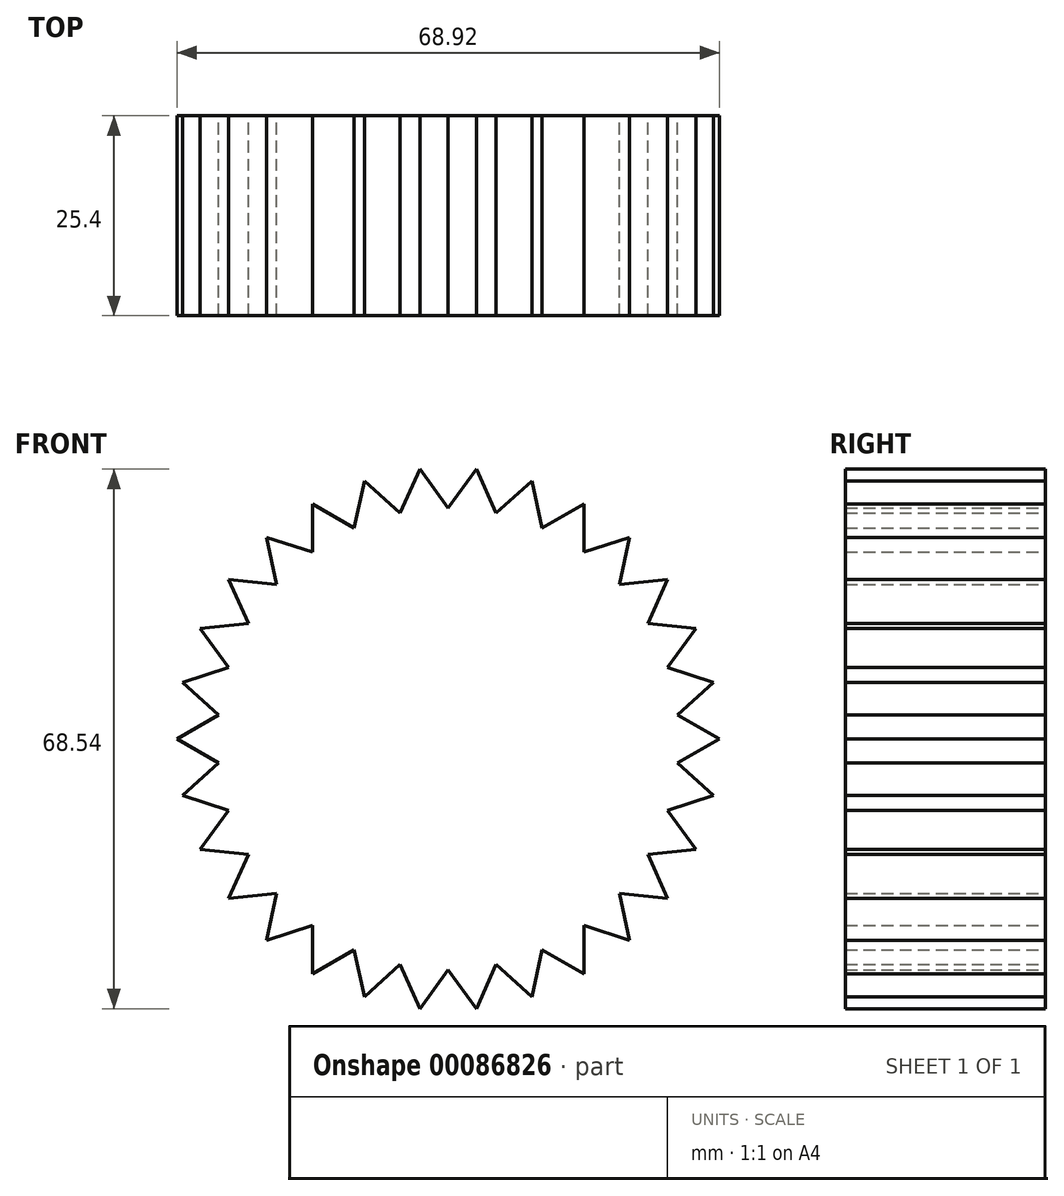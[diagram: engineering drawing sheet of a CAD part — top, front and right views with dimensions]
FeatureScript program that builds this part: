
annotation { "Feature Type Name" : "Feature", "Feature Type Description" : "" }
export const myFeature = defineFeature(function(context is Context, id is Id, definition is map)
    precondition{}
    {
        {
            var Q0;
            Q0=qCreatedBy(makeId("Front.planeOp"),FACE);
            var sketch = newSketch(context, id + "F0", { "sketchPlane" : qUnion([Q0])});
            skCircle(sketch, "E0.cCircle", {"center": v(0, 0) * mm, "radius": 29.31 * mm, "construction": true});
            skLineSegment(sketch, "E0.0", {"start": v(0, 29.31) * mm, "end": v(6.1, 28.67) * mm, "construction": true});
            skLineSegment(sketch, "E0.1", {"start": v(6.1, 28.67) * mm, "end": v(11.92, 26.78) * mm, "construction": true});
            skLineSegment(sketch, "E0.2", {"start": v(11.92, 26.78) * mm, "end": v(17.23, 23.71) * mm, "construction": true});
            skLineSegment(sketch, "E0.3", {"start": v(17.23, 23.71) * mm, "end": v(21.78, 19.61) * mm, "construction": true});
            skLineSegment(sketch, "E0.4", {"start": v(21.78, 19.61) * mm, "end": v(25.38, 14.66) * mm, "construction": true});
            skLineSegment(sketch, "E0.5", {"start": v(25.38, 14.66) * mm, "end": v(27.88, 9.06) * mm, "construction": true});
            skLineSegment(sketch, "E0.6", {"start": v(27.88, 9.06) * mm, "end": v(29.15, 3.06) * mm, "construction": true});
            skLineSegment(sketch, "E0.7", {"start": v(29.15, 3.06) * mm, "end": v(29.15, -3.06) * mm, "construction": true});
            skLineSegment(sketch, "E0.8", {"start": v(29.15, -3.06) * mm, "end": v(27.88, -9.06) * mm, "construction": true});
            skLineSegment(sketch, "E0.9", {"start": v(27.88, -9.06) * mm, "end": v(25.38, -14.66) * mm, "construction": true});
            skLineSegment(sketch, "E0.10", {"start": v(25.38, -14.66) * mm, "end": v(21.78, -19.61) * mm, "construction": true});
            skLineSegment(sketch, "E0.11", {"start": v(21.78, -19.61) * mm, "end": v(17.23, -23.71) * mm, "construction": true});
            skLineSegment(sketch, "E0.12", {"start": v(17.23, -23.71) * mm, "end": v(11.92, -26.78) * mm, "construction": true});
            skLineSegment(sketch, "E0.13", {"start": v(11.92, -26.78) * mm, "end": v(6.1, -28.67) * mm, "construction": true});
            skLineSegment(sketch, "E0.14", {"start": v(6.1, -28.67) * mm, "end": v(0, -29.31) * mm, "construction": true});
            skLineSegment(sketch, "E0.15", {"start": v(0, -29.31) * mm, "end": v(-6.1, -28.67) * mm, "construction": true});
            skLineSegment(sketch, "E0.16", {"start": v(-6.1, -28.67) * mm, "end": v(-11.92, -26.78) * mm, "construction": true});
            skLineSegment(sketch, "E0.17", {"start": v(-11.92, -26.78) * mm, "end": v(-17.23, -23.71) * mm, "construction": true});
            skLineSegment(sketch, "E0.18", {"start": v(-17.23, -23.71) * mm, "end": v(-21.78, -19.61) * mm, "construction": true});
            skLineSegment(sketch, "E0.19", {"start": v(-21.78, -19.61) * mm, "end": v(-25.38, -14.66) * mm, "construction": true});
            skLineSegment(sketch, "E0.20", {"start": v(-25.38, -14.66) * mm, "end": v(-27.88, -9.06) * mm, "construction": true});
            skLineSegment(sketch, "E0.21", {"start": v(-27.88, -9.06) * mm, "end": v(-29.15, -3.06) * mm, "construction": true});
            skLineSegment(sketch, "E0.22", {"start": v(-29.15, -3.06) * mm, "end": v(-29.15, 3.06) * mm, "construction": true});
            skLineSegment(sketch, "E0.23", {"start": v(-29.15, 3.06) * mm, "end": v(-27.88, 9.06) * mm, "construction": true});
            skLineSegment(sketch, "E0.24", {"start": v(-27.88, 9.06) * mm, "end": v(-25.38, 14.66) * mm, "construction": true});
            skLineSegment(sketch, "E0.25", {"start": v(-25.38, 14.66) * mm, "end": v(-21.78, 19.61) * mm, "construction": true});
            skLineSegment(sketch, "E0.26", {"start": v(-21.78, 19.61) * mm, "end": v(-17.23, 23.71) * mm, "construction": true});
            skLineSegment(sketch, "E0.27", {"start": v(-17.23, 23.71) * mm, "end": v(-11.92, 26.78) * mm, "construction": true});
            skLineSegment(sketch, "E0.28", {"start": v(-11.92, 26.78) * mm, "end": v(-6.1, 28.67) * mm, "construction": true});
            skLineSegment(sketch, "E0.29", {"start": v(-6.1, 28.67) * mm, "end": v(0, 29.31) * mm, "construction": true});
            skLineSegment(sketch, "E1", {"start": v(6.1, 28.67) * mm, "end": v(3.6, 34.27) * mm});
            skLineSegment(sketch, "E2", {"start": v(3.6, 34.27) * mm, "end": v(0, 29.31) * mm});
            skLineSegment(sketch, "E3.1.0", {"start": v(11.92, 26.78) * mm, "end": v(10.65, 32.77) * mm});
            skLineSegment(sketch, "E3.1.1", {"start": v(10.65, 32.77) * mm, "end": v(6.1, 28.67) * mm});
            skLineSegment(sketch, "E3.2.0", {"start": v(17.23, 23.71) * mm, "end": v(17.23, 29.84) * mm});
            skLineSegment(sketch, "E3.2.1", {"start": v(17.23, 29.84) * mm, "end": v(11.92, 26.78) * mm});
            skLineSegment(sketch, "E3.3.0", {"start": v(21.78, 19.61) * mm, "end": v(23.06, 25.6) * mm});
            skLineSegment(sketch, "E3.3.1", {"start": v(23.06, 25.6) * mm, "end": v(17.23, 23.71) * mm});
            skLineSegment(sketch, "E3.4.0", {"start": v(25.38, 14.66) * mm, "end": v(27.88, 20.25) * mm});
            skLineSegment(sketch, "E3.4.1", {"start": v(27.88, 20.25) * mm, "end": v(21.78, 19.61) * mm});
            skLineSegment(sketch, "E3.5.0", {"start": v(27.88, 9.06) * mm, "end": v(31.48, 14.01) * mm});
            skLineSegment(sketch, "E3.5.1", {"start": v(31.48, 14.01) * mm, "end": v(25.38, 14.66) * mm});
            skLineSegment(sketch, "E3.6.0", {"start": v(29.15, 3.06) * mm, "end": v(33.7, 7.16) * mm});
            skLineSegment(sketch, "E3.6.1", {"start": v(33.7, 7.16) * mm, "end": v(27.88, 9.06) * mm});
            skLineSegment(sketch, "E3.7.0", {"start": v(29.15, -3.06) * mm, "end": v(34.46, 0) * mm});
            skLineSegment(sketch, "E3.7.1", {"start": v(34.46, 0) * mm, "end": v(29.15, 3.06) * mm});
            skLineSegment(sketch, "E3.8.0", {"start": v(27.88, -9.06) * mm, "end": v(33.7, -7.16) * mm});
            skLineSegment(sketch, "E3.8.1", {"start": v(33.7, -7.16) * mm, "end": v(29.15, -3.06) * mm});
            skLineSegment(sketch, "E3.9.0", {"start": v(25.38, -14.66) * mm, "end": v(31.48, -14.01) * mm});
            skLineSegment(sketch, "E3.9.1", {"start": v(31.48, -14.01) * mm, "end": v(27.88, -9.06) * mm});
            skLineSegment(sketch, "E3.anchor1", {"start": v(0, 0) * mm, "end": v(6.1, 28.67) * mm, "construction": true});
            skLineSegment(sketch, "E3.anchor2", {"start": v(0, 0) * mm, "end": v(25.38, -14.66) * mm, "construction": true});
            skLineSegment(sketch, "E4.1.0", {"start": v(21.78, -19.61) * mm, "end": v(27.88, -20.25) * mm});
            skLineSegment(sketch, "E4.1.1", {"start": v(27.88, -20.25) * mm, "end": v(25.38, -14.66) * mm});
            skLineSegment(sketch, "E4.2.0", {"start": v(17.23, -23.71) * mm, "end": v(23.06, -25.6) * mm});
            skLineSegment(sketch, "E4.2.1", {"start": v(23.06, -25.6) * mm, "end": v(21.78, -19.61) * mm});
            skLineSegment(sketch, "E4.3.0", {"start": v(11.92, -26.78) * mm, "end": v(17.23, -29.84) * mm});
            skLineSegment(sketch, "E4.3.1", {"start": v(17.23, -29.84) * mm, "end": v(17.23, -23.71) * mm});
            skLineSegment(sketch, "E4.4.0", {"start": v(6.1, -28.67) * mm, "end": v(10.65, -32.77) * mm});
            skLineSegment(sketch, "E4.4.1", {"start": v(10.65, -32.77) * mm, "end": v(11.92, -26.78) * mm});
            skLineSegment(sketch, "E4.5.0", {"start": v(0, -29.31) * mm, "end": v(3.6, -34.27) * mm});
            skLineSegment(sketch, "E4.5.1", {"start": v(3.6, -34.27) * mm, "end": v(6.1, -28.67) * mm});
            skLineSegment(sketch, "E4.6.0", {"start": v(-6.1, -28.67) * mm, "end": v(-3.6, -34.27) * mm});
            skLineSegment(sketch, "E4.6.1", {"start": v(-3.6, -34.27) * mm, "end": v(0, -29.31) * mm});
            skLineSegment(sketch, "E4.7.0", {"start": v(-11.92, -26.78) * mm, "end": v(-10.65, -32.77) * mm});
            skLineSegment(sketch, "E4.7.1", {"start": v(-10.65, -32.77) * mm, "end": v(-6.1, -28.67) * mm});
            skLineSegment(sketch, "E4.8.0", {"start": v(-17.23, -23.71) * mm, "end": v(-17.23, -29.84) * mm});
            skLineSegment(sketch, "E4.8.1", {"start": v(-17.23, -29.84) * mm, "end": v(-11.92, -26.78) * mm});
            skLineSegment(sketch, "E4.9.0", {"start": v(-21.78, -19.61) * mm, "end": v(-23.06, -25.6) * mm});
            skLineSegment(sketch, "E4.9.1", {"start": v(-23.06, -25.6) * mm, "end": v(-17.23, -23.71) * mm});
            skLineSegment(sketch, "E4.anchor2", {"start": v(0, 0) * mm, "end": v(-21.78, -19.61) * mm, "construction": true});
            skLineSegment(sketch, "E5.1.0", {"start": v(-27.88, -20.25) * mm, "end": v(-21.78, -19.61) * mm});
            skLineSegment(sketch, "E5.1.1", {"start": v(-25.38, -14.66) * mm, "end": v(-27.88, -20.25) * mm});
            skLineSegment(sketch, "E5.2.0", {"start": v(-31.48, -14.01) * mm, "end": v(-25.38, -14.66) * mm});
            skLineSegment(sketch, "E5.2.1", {"start": v(-27.88, -9.06) * mm, "end": v(-31.48, -14.01) * mm});
            skLineSegment(sketch, "E5.3.0", {"start": v(-33.7, -7.16) * mm, "end": v(-27.88, -9.06) * mm});
            skLineSegment(sketch, "E5.3.1", {"start": v(-29.15, -3.06) * mm, "end": v(-33.7, -7.16) * mm});
            skLineSegment(sketch, "E5.4.0", {"start": v(-34.46, 0) * mm, "end": v(-29.15, -3.06) * mm});
            skLineSegment(sketch, "E5.4.1", {"start": v(-29.15, 3.06) * mm, "end": v(-34.46, 0) * mm});
            skLineSegment(sketch, "E5.5.0", {"start": v(-33.7, 7.16) * mm, "end": v(-29.15, 3.06) * mm});
            skLineSegment(sketch, "E5.5.1", {"start": v(-27.88, 9.06) * mm, "end": v(-33.7, 7.16) * mm});
            skLineSegment(sketch, "E5.6.0", {"start": v(-31.48, 14.01) * mm, "end": v(-27.88, 9.06) * mm});
            skLineSegment(sketch, "E5.6.1", {"start": v(-25.38, 14.66) * mm, "end": v(-31.48, 14.01) * mm});
            skLineSegment(sketch, "E5.7.0", {"start": v(-27.88, 20.25) * mm, "end": v(-25.38, 14.66) * mm});
            skLineSegment(sketch, "E5.7.1", {"start": v(-21.78, 19.61) * mm, "end": v(-27.88, 20.25) * mm});
            skLineSegment(sketch, "E5.8.0", {"start": v(-23.06, 25.6) * mm, "end": v(-21.78, 19.61) * mm});
            skLineSegment(sketch, "E5.8.1", {"start": v(-17.23, 23.71) * mm, "end": v(-23.06, 25.6) * mm});
            skLineSegment(sketch, "E5.9.0", {"start": v(-17.23, 29.84) * mm, "end": v(-17.23, 23.71) * mm});
            skLineSegment(sketch, "E5.9.1", {"start": v(-11.92, 26.78) * mm, "end": v(-17.23, 29.84) * mm});
            skLineSegment(sketch, "E5.anchor1", {"start": v(0, 0) * mm, "end": v(-23.06, -25.6) * mm, "construction": true});
            skLineSegment(sketch, "E5.anchor2", {"start": v(0, 0) * mm, "end": v(-17.23, 29.84) * mm, "construction": true});
            skLineSegment(sketch, "E6.1.0", {"start": v(-10.65, 32.77) * mm, "end": v(-11.92, 26.78) * mm});
            skLineSegment(sketch, "E6.1.1", {"start": v(-6.1, 28.67) * mm, "end": v(-10.65, 32.77) * mm});
            skLineSegment(sketch, "E6.2.0", {"start": v(-3.6, 34.27) * mm, "end": v(-6.1, 28.67) * mm});
            skLineSegment(sketch, "E6.2.1", {"start": v(0, 29.31) * mm, "end": v(-3.6, 34.27) * mm});
            skLineSegment(sketch, "E6.anchor1", {"start": v(0, 0) * mm, "end": v(-17.23, 23.71) * mm, "construction": true});
            skLineSegment(sketch, "E6.anchor2", {"start": v(0, 0) * mm, "end": v(-6.1, 28.67) * mm, "construction": true});
            skSolve(sketch);
        }
        {
            var Q0;
            Q0 = qSketchRegion(id + "F0", true);
            extrude(context, id + "F1", {"entities" : qUnion([Q0]), "depth" : 25.4 * mm});
        }
    });
